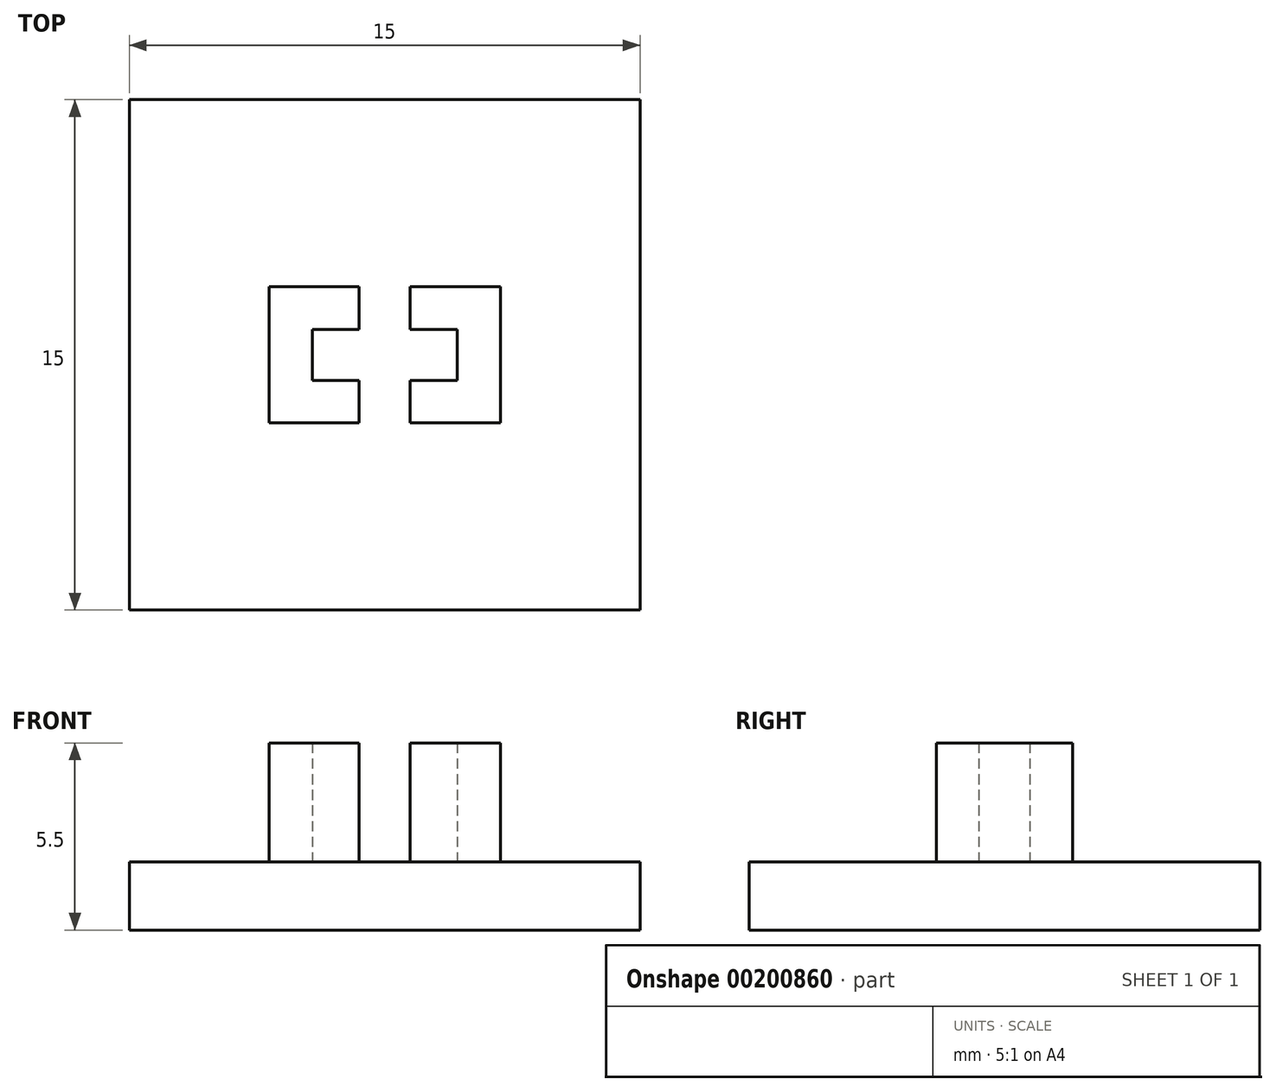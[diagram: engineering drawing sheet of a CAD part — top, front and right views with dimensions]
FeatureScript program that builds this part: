
annotation { "Feature Type Name" : "Feature", "Feature Type Description" : "" }
export const myFeature = defineFeature(function(context is Context, id is Id, definition is map)
    precondition{}
    {
        {
            var Q0;
            Q0=qCreatedBy(makeId("Top.planeOp"),FACE);
            var sketch = newSketch(context, id + "F0", { "sketchPlane" : qUnion([Q0])});
            skLineSegment(sketch, "E0.bottom", {"start": v(7.5, 7.5) * mm, "end": v(-7.5, 7.5) * mm});
            skLineSegment(sketch, "E0.top", {"start": v(7.5, -7.5) * mm, "end": v(-7.5, -7.5) * mm});
            skLineSegment(sketch, "E0.left", {"start": v(7.5, 7.5) * mm, "end": v(7.5, -7.5) * mm});
            skLineSegment(sketch, "E0.right", {"start": v(-7.5, 7.5) * mm, "end": v(-7.5, -7.5) * mm});
            skPoint(sketch, "E0.middle", {"position": v(0, 0) * mm});
            skSolve(sketch);
        }
        {
            var Q0;
            Q0 = qSketchRegion(id + "F0", true);
            var Q1;
            Q1=makeQuery(id+"F0.imprint","IMPRINT",FACE,{"disambiguationData":[TD([[makeQuery(id+"F0.imprint","IMPRINT",EDGE,{"derivedFrom":sQuery(id+"F0.wireOp",EDGE,"E0.bottom")}),1.0]])]});
            extrude(context, id + "F1", {"entities" : qUnion([Q0, Q1]), "depth" : 2 * mm});
        }
        {
            var Q0;
            Q0=makeQuery(id+"F1.opExtrude","CAP_FACE",FACE,{"disambiguationData":[OSD([sQuery(id+"F0.wireOp",EDGE,"E0.bottom"),sQuery(id+"F0.wireOp",EDGE,"E0.top"),sQuery(id+"F0.wireOp",EDGE,"E0.left"),sQuery(id+"F0.wireOp",EDGE,"E0.right")])],"isStart":false});
            var sketch = newSketch(context, id + "F2", { "sketchPlane" : qUnion([Q0])});
            skLineSegment(sketch, "E1.bottom", {"start": v(3.4, -2) * mm, "end": v(-3.4, -2) * mm});
            skLineSegment(sketch, "E1.top", {"start": v(3.4, 2) * mm, "end": v(-3.4, 2) * mm});
            skLineSegment(sketch, "E1.left", {"start": v(3.4, -2) * mm, "end": v(3.4, 2) * mm});
            skLineSegment(sketch, "E1.right", {"start": v(-3.4, -2) * mm, "end": v(-3.4, 2) * mm});
            skPoint(sketch, "E1.middle", {"position": v(0, 0) * mm});
            skLineSegment(sketch, "E2.bottom", {"start": v(0.75, -2) * mm, "end": v(-0.75, -2) * mm});
            skLineSegment(sketch, "E2.top", {"start": v(0.75, 2) * mm, "end": v(-0.75, 2) * mm});
            skLineSegment(sketch, "E2.left", {"start": v(0.75, -2) * mm, "end": v(0.75, 2) * mm});
            skLineSegment(sketch, "E2.right", {"start": v(-0.75, -2) * mm, "end": v(-0.75, 2) * mm});
            skLineSegment(sketch, "E3.bottom", {"start": v(2.13, -0.75) * mm, "end": v(-2.12, -0.75) * mm});
            skLineSegment(sketch, "E3.top", {"start": v(2.13, 0.75) * mm, "end": v(-2.12, 0.75) * mm});
            skLineSegment(sketch, "E3.left", {"start": v(2.13, -0.75) * mm, "end": v(2.13, 0.75) * mm});
            skLineSegment(sketch, "E3.right", {"start": v(-2.12, -0.75) * mm, "end": v(-2.12, 0.75) * mm});
            skSolve(sketch);
        }
        {
            var Q0;
            {var subQ0=sQuery(id+"F2.wireOp",EDGE,"E1.right");Q0=makeQuery(id+"F2.imprint","IMPRINT",FACE,{"disambiguationData":[TD([[makeQuery(id+"F2.imprint","IMPRINT",EDGE,{"derivedFrom":subQ0}),-1.0]])]});}
            var Q1;
            {var subQ0=sQuery(id+"F2.wireOp",EDGE,"E1.left");Q1=makeQuery(id+"F2.imprint","IMPRINT",FACE,{"disambiguationData":[TD([[makeQuery(id+"F2.imprint","IMPRINT",EDGE,{"derivedFrom":subQ0}),1.0]])]});}
            extrude(context, id + "F3", {"entities" : qUnion([Q0, Q1]), "operationType" : NewBodyOperationType.ADD, "depth" : 3.5 * mm});
        }
    });
